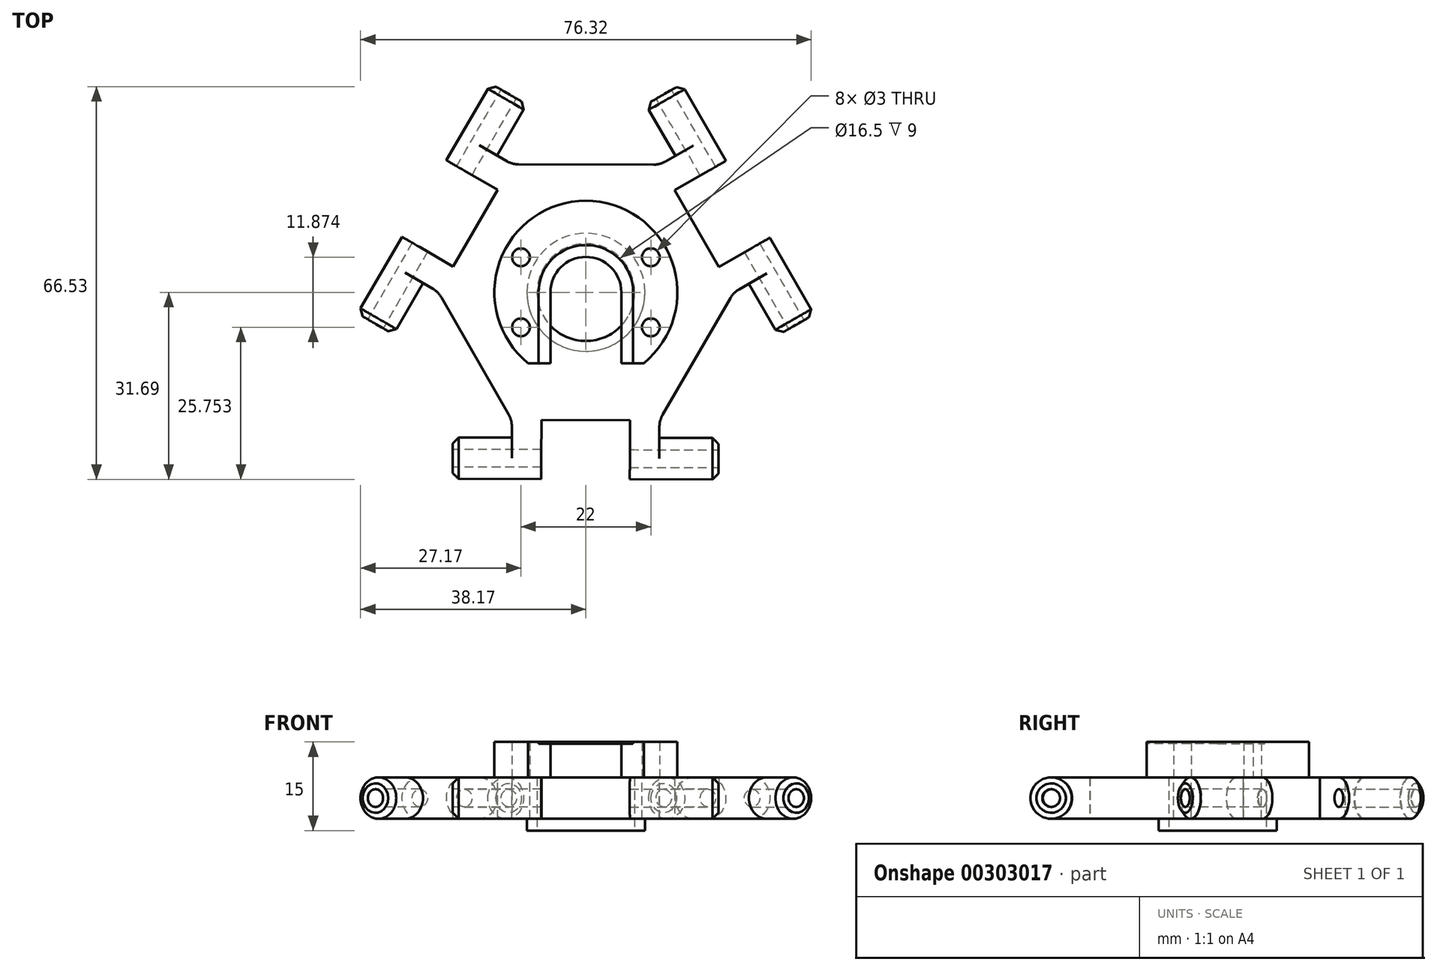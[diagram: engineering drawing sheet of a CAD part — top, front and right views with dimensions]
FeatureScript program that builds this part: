
annotation { "Feature Type Name" : "Feature", "Feature Type Description" : "" }
export const myFeature = defineFeature(function(context is Context, id is Id, definition is map)
    precondition{}
    {
        {
            var Q0;
            Q0=qCreatedBy(makeId("Top.planeOp"),FACE);
            var sketch = newSketch(context, id + "F0", { "sketchPlane" : qUnion([Q0])});
            skCircle(sketch, "E0", {"center": v(0, 0) * mm, "radius": 8.25 * mm});
            skCircle(sketch, "E1", {"center": v(0, 0) * mm, "radius": 11 * mm});
            skCircle(sketch, "E2.cCircle", {"center": v(0, 0) * mm, "radius": 11 * mm, "construction": true});
            skCircle(sketch, "E3.cCircle", {"center": v(0, 0) * mm, "radius": 21.65 * mm, "construction": true});
            skLineSegment(sketch, "E3.0", {"start": v(12.54, 21.63) * mm, "end": v(25, -0.05) * mm});
            skLineSegment(sketch, "E3.1", {"start": v(25, -0.05) * mm, "end": v(12.46, -21.67) * mm});
            skLineSegment(sketch, "E3.2", {"start": v(12.46, -21.67) * mm, "end": v(-12.54, -21.63) * mm});
            skLineSegment(sketch, "E3.3", {"start": v(-12.54, -21.63) * mm, "end": v(-25, 0.05) * mm});
            skLineSegment(sketch, "E3.4", {"start": v(-25, 0.05) * mm, "end": v(-12.46, 21.67) * mm});
            skLineSegment(sketch, "E3.5", {"start": v(-12.46, 21.67) * mm, "end": v(12.54, 21.63) * mm});
            skPoint(sketch, "E3.0.midPoint", {"position": v(18.77, 10.79) * mm});
            skSolve(sketch);
        }
        {
            var Q0;
            Q0=makeQuery(id+"F0.imprint","IMPRINT",FACE,{"disambiguationData":[TD([[makeQuery(id+"F0.imprint","IMPRINT",EDGE,{"derivedFrom":sQuery(id+"F0.wireOp",EDGE,"E1")}),-1.0]])]});
            var Q1;
            Q1=makeQuery(id+"F0.imprint","IMPRINT",FACE,{"disambiguationData":[TD([[makeQuery(id+"F0.imprint","IMPRINT",EDGE,{"derivedFrom":sQuery(id+"F0.wireOp",EDGE,"E0")}),-1.0]])]});
            extrude(context, id + "F1", {"entities" : qUnion([Q0, Q1]), "depth" : 7 * mm});
        }
        {
            var Q0;
            Q0=makeQuery(id+"F1.opExtrude","SWEPT_FACE",FACE,{"disambiguationData":[OSD([sQuery(id+"F0.wireOp",EDGE,"E3.2")])]});
            var sketch = newSketch(context, id + "F2", { "sketchPlane" : qUnion([Q0])});
            skLineSegment(sketch, "E4.bottom", {"start": v(-12.5, 7) * mm, "end": v(-7.5, 7) * mm});
            skLineSegment(sketch, "E4.top", {"start": v(-12.5, 0) * mm, "end": v(-7.5, 0) * mm});
            skLineSegment(sketch, "E4.left", {"start": v(-12.5, 7) * mm, "end": v(-12.5, 0) * mm});
            skLineSegment(sketch, "E4.right", {"start": v(-7.5, 7) * mm, "end": v(-7.5, 0) * mm});
            skLineSegment(sketch, "E5.bottom", {"start": v(12.5, 7) * mm, "end": v(7.5, 7) * mm});
            skLineSegment(sketch, "E5.top", {"start": v(12.5, 0) * mm, "end": v(7.5, 0) * mm});
            skLineSegment(sketch, "E5.left", {"start": v(12.5, 7) * mm, "end": v(12.5, 0) * mm});
            skLineSegment(sketch, "E5.right", {"start": v(7.5, 7) * mm, "end": v(7.5, 0) * mm});
            skSolve(sketch);
        }
        {
            var Q0;
            Q0=makeQuery(id+"F2.imprint","IMPRINT",FACE,{"disambiguationData":[TD([[makeQuery(id+"F2.imprint","IMPRINT",EDGE,{"derivedFrom":sQuery(id+"F2.wireOp",EDGE,"E4.bottom")}),1.0]])]});
            var Q1;
            Q1=makeQuery(id+"F2.imprint","IMPRINT",FACE,{"disambiguationData":[TD([[makeQuery(id+"F2.imprint","IMPRINT",EDGE,{"derivedFrom":sQuery(id+"F2.wireOp",EDGE,"E5.bottom")}),1.0]])]});
            extrude(context, id + "F3", {"entities" : qUnion([Q0, Q1]), "operationType" : NewBodyOperationType.ADD, "depth" : 10 * mm});
        }
        {
            var Q0;
            Q0=makeQuery(id+"F3.opExtrude","SWEPT_FACE",FACE,{"disambiguationData":[OSD([sQuery(id+"F2.wireOp",EDGE,"E4.left")])]});
            var sketch = newSketch(context, id + "F4", { "sketchPlane" : qUnion([Q0])});
            skCircle(sketch, "E6", {"center": v(28.15, 3.5) * mm, "radius": 3.5 * mm});
            skPoint(sketch, "E6.centerSnap0", {"position": v(28.15, 0) * mm});
            skPoint(sketch, "E6.centerSnap1", {"position": v(21.65, 3.5) * mm});
            skLineSegment(sketch, "E7", {"start": v(31.65, 3.5) * mm, "end": v(28.15, 3.5) * mm, "construction": true});
            skSolve(sketch);
        }
        {
            var Q0;
            {var subQ0=sQuery(id+"F4.wireOp",EDGE,"E6");var subQ1=sQuery(id+"F2.wireOp",EDGE,"E4.left");var subQ3=makeQuery(id+"F4.imprint","INTERSECT",VERTEX,{"derivedFrom":[makeQuery(id+"F3.opExtrude","CAP_EDGE",EDGE,{"disambiguationData":[OSD([subQ1])],"isStart":false}),subQ0]});Q0=makeQuery(id+"F4.imprint","IMPRINT",FACE,{"disambiguationData":[TD([[makeQuery(id+"F4.imprint","IMPRINT",EDGE,{"disambiguationData":[TD([[subQ3,-1.0]])],"derivedFrom":subQ0}),1.0]])]});}
            extrude(context, id + "F5", {"entities" : qUnion([Q0]), "operationType" : NewBodyOperationType.ADD, "depth" : 10 * mm, "offsetDistance" : 25 * mm});
        }
        {
            var Q0;
            Q0=makeQuery(id+"F5.opExtrude","CAP_FACE",FACE,{"disambiguationData":[OSD([sQuery(id+"F4.wireOp",EDGE,"E6")])],"isStart":false});
            var sketch = newSketch(context, id + "F6", { "sketchPlane" : qUnion([Q0])});
            skCircle(sketch, "E8", {"center": v(28.15, 3.5) * mm, "radius": 1.5 * mm});
            skSolve(sketch);
        }
        {
            var Q0;
            Q0=makeQuery(id+"F6.imprint","IMPRINT",FACE,{"disambiguationData":[TD([[makeQuery(id+"F6.imprint","IMPRINT",EDGE,{"derivedFrom":sQuery(id+"F6.wireOp",EDGE,"E8")}),1.0]])]});
            extrude(context, id + "F7", {"entities" : qUnion([Q0]), "operationType" : NewBodyOperationType.REMOVE, "oppositeDirection" : true, "depth" : 25 * mm});
        }
        {
            var Q0;
            Q0=makeQuery(id+"F5.opExtrude","CAP_EDGE",EDGE,{"disambiguationData":[OSD([sQuery(id+"F4.wireOp",EDGE,"E6")])],"isStart":false});
            chamfer(context, id + "F8", {"entities" : qUnion([Q0]), "width" : 1 * mm, "tangentPropagation" : true});
        }
        {
            var Q0;
            Q0=makeQuery(id+"F3.opExtrude","SWEPT_FACE",FACE,{"disambiguationData":[OSD([sQuery(id+"F2.wireOp",EDGE,"E5.left")])]});
            var sketch = newSketch(context, id + "F9", { "sketchPlane" : qUnion([Q0])});
            skCircle(sketch, "E9", {"center": v(-28.15, 3.5) * mm, "radius": 3.5 * mm});
            skPoint(sketch, "E9.centerSnap0", {"position": v(-31.65, 3.5) * mm});
            skPoint(sketch, "E9.centerSnap1", {"position": v(-28.15, 5) * mm});
            skLineSegment(sketch, "E10", {"start": v(-31.65, 3.5) * mm, "end": v(-28.15, 3.5) * mm, "construction": true});
            skSolve(sketch);
        }
        {
            var Q0;
            {var subQ0=sQuery(id+"F9.wireOp",EDGE,"E9");var subQ1=sQuery(id+"F2.wireOp",EDGE,"E5.left");var subQ4=makeQuery(id+"F9.imprint","INTERSECT",VERTEX,{"derivedFrom":[makeQuery(id+"F3.opExtrude","CAP_EDGE",EDGE,{"disambiguationData":[OSD([subQ1])],"isStart":false}),subQ0]});Q0=makeQuery(id+"F9.imprint","IMPRINT",FACE,{"disambiguationData":[TD([[makeQuery(id+"F9.imprint","IMPRINT",EDGE,{"disambiguationData":[TD([[subQ4,1.0]])],"derivedFrom":subQ0}),1.0]])]});}
            extrude(context, id + "F10", {"entities" : qUnion([Q0]), "operationType" : NewBodyOperationType.ADD, "depth" : 10 * mm, "offsetDistance" : 25 * mm});
        }
        {
            var Q0;
            Q0=makeQuery(id+"F10.opExtrude","CAP_FACE",FACE,{"disambiguationData":[OSD([sQuery(id+"F9.wireOp",EDGE,"E9")])],"isStart":false});
            var sketch = newSketch(context, id + "F11", { "sketchPlane" : qUnion([Q0])});
            skCircle(sketch, "E11", {"center": v(-28.15, 3.5) * mm, "radius": 1.5 * mm});
            skSolve(sketch);
        }
        {
            var Q0;
            Q0=makeQuery(id+"F11.imprint","IMPRINT",FACE,{"disambiguationData":[TD([[makeQuery(id+"F11.imprint","IMPRINT",EDGE,{"derivedFrom":sQuery(id+"F11.wireOp",EDGE,"E11")}),1.0]])]});
            extrude(context, id + "F12", {"entities" : qUnion([Q0]), "operationType" : NewBodyOperationType.REMOVE, "oppositeDirection" : true, "depth" : 25 * mm});
        }
        {
            var Q0;
            Q0=makeQuery(id+"F10.opExtrude","CAP_EDGE",EDGE,{"disambiguationData":[OSD([sQuery(id+"F9.wireOp",EDGE,"E9")])],"isStart":false});
            chamfer(context, id + "F13", {"entities" : qUnion([Q0]), "width" : 1 * mm, "tangentPropagation" : true});
        }
        {
            var Q0;
            Q0=makeQuery(id+"F1.opExtrude","SWEPT_FACE",FACE,{"disambiguationData":[OSD([sQuery(id+"F0.wireOp",EDGE,"E3.0")])]});
            var sketch = newSketch(context, id + "F14", { "sketchPlane" : qUnion([Q0])});
            skLineSegment(sketch, "E12.bottom", {"start": v(-12.5, 7) * mm, "end": v(-7.5, 7) * mm});
            skLineSegment(sketch, "E12.top", {"start": v(-12.5, 0) * mm, "end": v(-7.5, 0) * mm});
            skLineSegment(sketch, "E12.left", {"start": v(-12.5, 7) * mm, "end": v(-12.5, 0) * mm});
            skLineSegment(sketch, "E12.right", {"start": v(-7.5, 7) * mm, "end": v(-7.5, 0) * mm});
            skLineSegment(sketch, "E13.bottom", {"start": v(12.5, 7) * mm, "end": v(7.5, 7) * mm});
            skLineSegment(sketch, "E13.top", {"start": v(12.5, 0) * mm, "end": v(7.5, 0) * mm});
            skLineSegment(sketch, "E13.left", {"start": v(12.5, 7) * mm, "end": v(12.5, 0) * mm});
            skLineSegment(sketch, "E13.right", {"start": v(7.5, 7) * mm, "end": v(7.5, 0) * mm});
            skSolve(sketch);
        }
        {
            var Q0;
            Q0=makeQuery(id+"F14.imprint","IMPRINT",FACE,{"disambiguationData":[TD([[makeQuery(id+"F14.imprint","IMPRINT",EDGE,{"derivedFrom":sQuery(id+"F14.wireOp",EDGE,"E12.bottom")}),1.0]])]});
            var Q1;
            Q1=makeQuery(id+"F14.imprint","IMPRINT",FACE,{"disambiguationData":[TD([[makeQuery(id+"F14.imprint","IMPRINT",EDGE,{"derivedFrom":sQuery(id+"F14.wireOp",EDGE,"E13.bottom")}),1.0]])]});
            extrude(context, id + "F15", {"entities" : qUnion([Q0, Q1]), "operationType" : NewBodyOperationType.ADD, "depth" : 10 * mm});
        }
        {
            var Q0;
            Q0=makeQuery(id+"F15.opExtrude","SWEPT_FACE",FACE,{"disambiguationData":[OSD([sQuery(id+"F14.wireOp",EDGE,"E12.left")])]});
            var sketch = newSketch(context, id + "F16", { "sketchPlane" : qUnion([Q0])});
            skCircle(sketch, "E14", {"center": v(28.15, 3.5) * mm, "radius": 3.5 * mm});
            skPoint(sketch, "E14.centerSnap0", {"position": v(31.65, 3.5) * mm});
            skPoint(sketch, "E14.centerSnap1", {"position": v(28.15, 5) * mm});
            skLineSegment(sketch, "E15", {"start": v(31.65, 3.5) * mm, "end": v(28.15, 3.5) * mm, "construction": true});
            skSolve(sketch);
        }
        {
            var Q0;
            {var subQ0=sQuery(id+"F16.wireOp",EDGE,"E14");var subQ1=sQuery(id+"F14.wireOp",EDGE,"E12.left");var subQ3=makeQuery(id+"F16.imprint","INTERSECT",VERTEX,{"derivedFrom":[makeQuery(id+"F15.opExtrude","CAP_EDGE",EDGE,{"disambiguationData":[OSD([subQ1])],"isStart":false}),subQ0]});Q0=makeQuery(id+"F16.imprint","IMPRINT",FACE,{"disambiguationData":[TD([[makeQuery(id+"F16.imprint","IMPRINT",EDGE,{"disambiguationData":[TD([[subQ3,-1.0]])],"derivedFrom":subQ0}),1.0]])]});}
            extrude(context, id + "F17", {"entities" : qUnion([Q0]), "operationType" : NewBodyOperationType.ADD, "depth" : 10 * mm, "offsetDistance" : 25 * mm});
        }
        {
            var Q0;
            Q0=makeQuery(id+"F17.opExtrude","CAP_FACE",FACE,{"disambiguationData":[OSD([sQuery(id+"F16.wireOp",EDGE,"E14")])],"isStart":false});
            var sketch = newSketch(context, id + "F18", { "sketchPlane" : qUnion([Q0])});
            skCircle(sketch, "E16", {"center": v(28.15, 3.5) * mm, "radius": 1.5 * mm});
            skSolve(sketch);
        }
        {
            var Q0;
            Q0=makeQuery(id+"F18.imprint","IMPRINT",FACE,{"disambiguationData":[TD([[makeQuery(id+"F18.imprint","IMPRINT",EDGE,{"derivedFrom":sQuery(id+"F18.wireOp",EDGE,"E16")}),1.0]])]});
            extrude(context, id + "F19", {"entities" : qUnion([Q0]), "operationType" : NewBodyOperationType.REMOVE, "oppositeDirection" : true, "depth" : 25 * mm});
        }
        {
            var Q0;
            Q0=makeQuery(id+"F17.opExtrude","CAP_EDGE",EDGE,{"disambiguationData":[OSD([sQuery(id+"F16.wireOp",EDGE,"E14")])],"isStart":false});
            chamfer(context, id + "F20", {"entities" : qUnion([Q0]), "width" : 1 * mm, "tangentPropagation" : true});
        }
        {
            var Q0;
            Q0=makeQuery(id+"F15.opExtrude","SWEPT_FACE",FACE,{"disambiguationData":[OSD([sQuery(id+"F14.wireOp",EDGE,"E13.left")])]});
            var sketch = newSketch(context, id + "F21", { "sketchPlane" : qUnion([Q0])});
            skCircle(sketch, "E17", {"center": v(-28.15, 3.5) * mm, "radius": 3.5 * mm});
            skPoint(sketch, "E17.centerSnap0", {"position": v(-28.15, 5) * mm});
            skPoint(sketch, "E17.centerSnap1", {"position": v(-21.65, 3.5) * mm});
            skLineSegment(sketch, "E18", {"start": v(-31.65, 3.5) * mm, "end": v(-28.15, 3.5) * mm, "construction": true});
            skPoint(sketch, "E18.endSnap0", {"position": v(-31.65, 3.5) * mm});
            skSolve(sketch);
        }
        {
            var Q0;
            {var subQ0=sQuery(id+"F21.wireOp",EDGE,"E17");var subQ1=sQuery(id+"F14.wireOp",EDGE,"E13.left");var subQ4=makeQuery(id+"F21.imprint","INTERSECT",VERTEX,{"derivedFrom":[makeQuery(id+"F15.opExtrude","CAP_EDGE",EDGE,{"disambiguationData":[OSD([subQ1])],"isStart":false}),subQ0]});Q0=makeQuery(id+"F21.imprint","IMPRINT",FACE,{"disambiguationData":[TD([[makeQuery(id+"F21.imprint","IMPRINT",EDGE,{"disambiguationData":[TD([[subQ4,1.0]])],"derivedFrom":subQ0}),1.0]])]});}
            extrude(context, id + "F22", {"entities" : qUnion([Q0]), "operationType" : NewBodyOperationType.ADD, "depth" : 10 * mm, "offsetDistance" : 25 * mm});
        }
        {
            var Q0;
            Q0=makeQuery(id+"F22.opExtrude","CAP_FACE",FACE,{"disambiguationData":[OSD([sQuery(id+"F21.wireOp",EDGE,"E17")])],"isStart":false});
            var sketch = newSketch(context, id + "F23", { "sketchPlane" : qUnion([Q0])});
            skCircle(sketch, "E19", {"center": v(-28.15, 3.5) * mm, "radius": 1.5 * mm});
            skSolve(sketch);
        }
        {
            var Q0;
            Q0=makeQuery(id+"F23.imprint","IMPRINT",FACE,{"disambiguationData":[TD([[makeQuery(id+"F23.imprint","IMPRINT",EDGE,{"derivedFrom":sQuery(id+"F23.wireOp",EDGE,"E19")}),1.0]])]});
            extrude(context, id + "F24", {"entities" : qUnion([Q0]), "operationType" : NewBodyOperationType.REMOVE, "oppositeDirection" : true, "depth" : 25 * mm});
        }
        {
            var Q0;
            Q0=makeQuery(id+"F22.opExtrude","CAP_EDGE",EDGE,{"disambiguationData":[OSD([sQuery(id+"F21.wireOp",EDGE,"E17")])],"isStart":false});
            chamfer(context, id + "F25", {"entities" : qUnion([Q0]), "width" : 1 * mm, "tangentPropagation" : true});
        }
        {
            var Q0;
            Q0=makeQuery(id+"F1.opExtrude","SWEPT_FACE",FACE,{"disambiguationData":[OSD([sQuery(id+"F0.wireOp",EDGE,"E3.4")])]});
            var sketch = newSketch(context, id + "F26", { "sketchPlane" : qUnion([Q0])});
            skLineSegment(sketch, "E20.bottom", {"start": v(12.5, 0) * mm, "end": v(7.5, 0) * mm});
            skLineSegment(sketch, "E20.top", {"start": v(12.5, 7) * mm, "end": v(7.5, 7) * mm});
            skLineSegment(sketch, "E20.left", {"start": v(12.5, 0) * mm, "end": v(12.5, 7) * mm});
            skLineSegment(sketch, "E20.right", {"start": v(7.5, 0) * mm, "end": v(7.5, 7) * mm});
            skLineSegment(sketch, "E21.bottom", {"start": v(-12.5, 0) * mm, "end": v(-7.5, 0) * mm});
            skLineSegment(sketch, "E21.top", {"start": v(-12.5, 7) * mm, "end": v(-7.5, 7) * mm});
            skLineSegment(sketch, "E21.left", {"start": v(-12.5, 0) * mm, "end": v(-12.5, 7) * mm});
            skLineSegment(sketch, "E21.right", {"start": v(-7.5, 0) * mm, "end": v(-7.5, 7) * mm});
            skSolve(sketch);
        }
        {
            var Q0;
            Q0=makeQuery(id+"F26.imprint","IMPRINT",FACE,{"disambiguationData":[TD([[makeQuery(id+"F26.imprint","IMPRINT",EDGE,{"derivedFrom":sQuery(id+"F26.wireOp",EDGE,"E20.bottom")}),-1.0]])]});
            var Q1;
            Q1=makeQuery(id+"F26.imprint","IMPRINT",FACE,{"disambiguationData":[TD([[makeQuery(id+"F26.imprint","IMPRINT",EDGE,{"derivedFrom":sQuery(id+"F26.wireOp",EDGE,"E21.bottom")}),-1.0]])]});
            extrude(context, id + "F27", {"entities" : qUnion([Q0, Q1]), "operationType" : NewBodyOperationType.ADD, "depth" : 10 * mm});
        }
        {
            var Q0;
            Q0=makeQuery(id+"F27.opExtrude","SWEPT_FACE",FACE,{"disambiguationData":[OSD([sQuery(id+"F26.wireOp",EDGE,"E21.left")])]});
            var sketch = newSketch(context, id + "F28", { "sketchPlane" : qUnion([Q0])});
            skCircle(sketch, "E22", {"center": v(28.15, 3.5) * mm, "radius": 3.5 * mm});
            skPoint(sketch, "E22.centerSnap0", {"position": v(31.65, 3.5) * mm});
            skPoint(sketch, "E22.centerSnap1", {"position": v(28.15, 0) * mm});
            skLineSegment(sketch, "E23", {"start": v(31.65, 3.5) * mm, "end": v(28.15, 3.5) * mm, "construction": true});
            skSolve(sketch);
        }
        {
            var Q0;
            {var subQ0=sQuery(id+"F28.wireOp",EDGE,"E22");var subQ1=sQuery(id+"F26.wireOp",EDGE,"E21.left");var subQ3=makeQuery(id+"F28.imprint","INTERSECT",VERTEX,{"derivedFrom":[makeQuery(id+"F27.opExtrude","CAP_EDGE",EDGE,{"disambiguationData":[OSD([subQ1])],"isStart":false}),subQ0]});Q0=makeQuery(id+"F28.imprint","IMPRINT",FACE,{"disambiguationData":[TD([[makeQuery(id+"F28.imprint","IMPRINT",EDGE,{"disambiguationData":[TD([[subQ3,-1.0]])],"derivedFrom":subQ0}),1.0]])]});}
            extrude(context, id + "F29", {"entities" : qUnion([Q0]), "operationType" : NewBodyOperationType.ADD, "depth" : 10 * mm, "offsetDistance" : 25 * mm});
        }
        {
            var Q0;
            Q0=makeQuery(id+"F29.opExtrude","CAP_FACE",FACE,{"disambiguationData":[OSD([sQuery(id+"F28.wireOp",EDGE,"E22")])],"isStart":false});
            var sketch = newSketch(context, id + "F30", { "sketchPlane" : qUnion([Q0])});
            skCircle(sketch, "E24", {"center": v(28.15, 3.5) * mm, "radius": 1.5 * mm});
            skSolve(sketch);
        }
        {
            var Q0;
            Q0=makeQuery(id+"F30.imprint","IMPRINT",FACE,{"disambiguationData":[TD([[makeQuery(id+"F30.imprint","IMPRINT",EDGE,{"derivedFrom":sQuery(id+"F30.wireOp",EDGE,"E24")}),1.0]])]});
            extrude(context, id + "F31", {"entities" : qUnion([Q0]), "operationType" : NewBodyOperationType.REMOVE, "oppositeDirection" : true, "depth" : 25 * mm});
        }
        {
            var Q0;
            Q0=makeQuery(id+"F29.opExtrude","CAP_EDGE",EDGE,{"disambiguationData":[OSD([sQuery(id+"F28.wireOp",EDGE,"E22")])],"isStart":false});
            chamfer(context, id + "F32", {"entities" : qUnion([Q0]), "width" : 1 * mm, "tangentPropagation" : true});
        }
        {
            var Q0;
            Q0=makeQuery(id+"F27.opExtrude","SWEPT_FACE",FACE,{"disambiguationData":[OSD([sQuery(id+"F26.wireOp",EDGE,"E20.left")])]});
            var sketch = newSketch(context, id + "F33", { "sketchPlane" : qUnion([Q0])});
            skCircle(sketch, "E25", {"center": v(-28.15, 3.5) * mm, "radius": 3.5 * mm});
            skPoint(sketch, "E25.centerSnap0", {"position": v(-28.15, 5) * mm});
            skPoint(sketch, "E25.centerSnap1", {"position": v(-21.65, 3.5) * mm});
            skLineSegment(sketch, "E26", {"start": v(-31.65, 3.5) * mm, "end": v(-28.15, 3.5) * mm, "construction": true});
            skSolve(sketch);
        }
        {
            var Q0;
            {var subQ0=sQuery(id+"F33.wireOp",EDGE,"E25");var subQ1=sQuery(id+"F26.wireOp",EDGE,"E20.left");var subQ4=makeQuery(id+"F33.imprint","INTERSECT",VERTEX,{"derivedFrom":[makeQuery(id+"F27.opExtrude","CAP_EDGE",EDGE,{"disambiguationData":[OSD([subQ1])],"isStart":false}),subQ0]});Q0=makeQuery(id+"F33.imprint","IMPRINT",FACE,{"disambiguationData":[TD([[makeQuery(id+"F33.imprint","IMPRINT",EDGE,{"disambiguationData":[TD([[subQ4,1.0]])],"derivedFrom":subQ0}),1.0]])]});}
            extrude(context, id + "F34", {"entities" : qUnion([Q0]), "operationType" : NewBodyOperationType.ADD, "depth" : 10 * mm, "offsetDistance" : 25 * mm});
        }
        {
            var Q0;
            Q0=makeQuery(id+"F34.opExtrude","CAP_FACE",FACE,{"disambiguationData":[OSD([sQuery(id+"F33.wireOp",EDGE,"E25")])],"isStart":false});
            var sketch = newSketch(context, id + "F35", { "sketchPlane" : qUnion([Q0])});
            skCircle(sketch, "E27", {"center": v(-28.15, 3.5) * mm, "radius": 1.5 * mm});
            skSolve(sketch);
        }
        {
            var Q0;
            Q0=makeQuery(id+"F35.imprint","IMPRINT",FACE,{"disambiguationData":[TD([[makeQuery(id+"F35.imprint","IMPRINT",EDGE,{"derivedFrom":sQuery(id+"F35.wireOp",EDGE,"E27")}),1.0]])]});
            extrude(context, id + "F36", {"entities" : qUnion([Q0]), "operationType" : NewBodyOperationType.REMOVE, "oppositeDirection" : true, "depth" : 25 * mm});
        }
        {
            var Q0;
            Q0=makeQuery(id+"F34.opExtrude","CAP_EDGE",EDGE,{"disambiguationData":[OSD([sQuery(id+"F33.wireOp",EDGE,"E25")])],"isStart":false});
            chamfer(context, id + "F37", {"entities" : qUnion([Q0]), "width" : 1 * mm, "tangentPropagation" : true});
        }
        {
            var Q0;
            Q0=makeQuery(id+"F27.boolean.opBoolean","MERGE",FACE,{"derivedFrom":[makeQuery(id+"F15.boolean.opBoolean","MERGE",FACE,{"derivedFrom":[makeQuery(id+"F3.boolean.opBoolean","MERGE",FACE,{"derivedFrom":[makeQuery(id+"F1.opExtrude","CAP_FACE",FACE,{"disambiguationData":[OSD([sQuery(id+"F0.wireOp",EDGE,"E0"),sQuery(id+"F0.wireOp",EDGE,"E3.0"),sQuery(id+"F0.wireOp",EDGE,"E3.1"),sQuery(id+"F0.wireOp",EDGE,"E3.2"),sQuery(id+"F0.wireOp",EDGE,"E3.3"),sQuery(id+"F0.wireOp",EDGE,"E3.4"),sQuery(id+"F0.wireOp",EDGE,"E3.5")])],"isStart":false}),makeQuery(id+"F3.opExtrude","SWEPT_FACE",FACE,{"disambiguationData":[OSD([sQuery(id+"F2.wireOp",EDGE,"E4.bottom")])]}),makeQuery(id+"F3.opExtrude","SWEPT_FACE",FACE,{"disambiguationData":[OSD([sQuery(id+"F2.wireOp",EDGE,"E5.bottom")])]})]}),makeQuery(id+"F15.opExtrude","SWEPT_FACE",FACE,{"disambiguationData":[OSD([sQuery(id+"F14.wireOp",EDGE,"E12.bottom")])]}),makeQuery(id+"F15.opExtrude","SWEPT_FACE",FACE,{"disambiguationData":[OSD([sQuery(id+"F14.wireOp",EDGE,"E13.bottom")])]})]}),makeQuery(id+"F27.opExtrude","SWEPT_FACE",FACE,{"disambiguationData":[OSD([sQuery(id+"F26.wireOp",EDGE,"E20.top")])]}),makeQuery(id+"F27.opExtrude","SWEPT_FACE",FACE,{"disambiguationData":[OSD([sQuery(id+"F26.wireOp",EDGE,"E21.top")])]})]});
            var sketch = newSketch(context, id + "F38", { "sketchPlane" : qUnion([Q0])});
            skLineSegment(sketch, "E28.bottom", {"start": v(11, 5.94) * mm, "end": v(-11, 5.94) * mm, "construction": true});
            skLineSegment(sketch, "E28.top", {"start": v(11, -5.94) * mm, "end": v(-11, -5.94) * mm, "construction": true});
            skLineSegment(sketch, "E28.left", {"start": v(11, 5.94) * mm, "end": v(11, -5.94) * mm, "construction": true});
            skLineSegment(sketch, "E28.right", {"start": v(-11, 5.94) * mm, "end": v(-11, -5.94) * mm, "construction": true});
            skPoint(sketch, "E28.middle", {"position": v(0, 0) * mm});
            skCircle(sketch, "E29", {"center": v(-11, 5.94) * mm, "radius": 1.5 * mm});
            skCircle(sketch, "E30", {"center": v(11, 5.94) * mm, "radius": 1.5 * mm});
            skCircle(sketch, "E31", {"center": v(11, -5.94) * mm, "radius": 1.5 * mm});
            skCircle(sketch, "E32", {"center": v(-11, -5.94) * mm, "radius": 1.5 * mm});
            skSolve(sketch);
        }
        {
            var Q0;
            Q0=makeQuery(id+"F38.imprint","IMPRINT",FACE,{"disambiguationData":[TD([[makeQuery(id+"F38.imprint","IMPRINT",EDGE,{"derivedFrom":sQuery(id+"F38.wireOp",EDGE,"E29")}),1.0]])]});
            var Q1;
            Q1=makeQuery(id+"F38.imprint","IMPRINT",FACE,{"disambiguationData":[TD([[makeQuery(id+"F38.imprint","IMPRINT",EDGE,{"derivedFrom":sQuery(id+"F38.wireOp",EDGE,"E30")}),1.0]])]});
            var Q2;
            Q2=makeQuery(id+"F38.imprint","IMPRINT",FACE,{"disambiguationData":[TD([[makeQuery(id+"F38.imprint","IMPRINT",EDGE,{"derivedFrom":sQuery(id+"F38.wireOp",EDGE,"E31")}),1.0]])]});
            var Q3;
            Q3=makeQuery(id+"F38.imprint","IMPRINT",FACE,{"disambiguationData":[TD([[makeQuery(id+"F38.imprint","IMPRINT",EDGE,{"derivedFrom":sQuery(id+"F38.wireOp",EDGE,"E32")}),1.0]])]});
            extrude(context, id + "F39", {"entities" : qUnion([Q0, Q1, Q2, Q3]), "operationType" : NewBodyOperationType.REMOVE, "oppositeDirection" : true, "depth" : 25 * mm});
        }
        {
            var Q0;
            Q0=makeQuery(id+"F3.opExtrude","CAP_EDGE",EDGE,{"disambiguationData":[OSD([sQuery(id+"F2.wireOp",EDGE,"E4.bottom")])],"isStart":false});
            var Q1;
            Q1=makeQuery(id+"F3.opExtrude","CAP_EDGE",EDGE,{"disambiguationData":[OSD([sQuery(id+"F2.wireOp",EDGE,"E4.top")])],"isStart":false});
            var Q2;
            Q2=makeQuery(id+"F3.opExtrude","CAP_EDGE",EDGE,{"disambiguationData":[OSD([sQuery(id+"F2.wireOp",EDGE,"E5.top")])],"isStart":false});
            var Q3;
            Q3=makeQuery(id+"F3.opExtrude","CAP_EDGE",EDGE,{"disambiguationData":[OSD([sQuery(id+"F2.wireOp",EDGE,"E5.bottom")])],"isStart":false});
            var Q4;
            Q4=makeQuery(id+"F15.opExtrude","CAP_EDGE",EDGE,{"disambiguationData":[OSD([sQuery(id+"F14.wireOp",EDGE,"E12.top")])],"isStart":false});
            var Q5;
            Q5=makeQuery(id+"F15.opExtrude","CAP_EDGE",EDGE,{"disambiguationData":[OSD([sQuery(id+"F14.wireOp",EDGE,"E12.bottom")])],"isStart":false});
            var Q6;
            Q6=makeQuery(id+"F15.opExtrude","CAP_EDGE",EDGE,{"disambiguationData":[OSD([sQuery(id+"F14.wireOp",EDGE,"E13.top")])],"isStart":false});
            var Q7;
            Q7=makeQuery(id+"F15.opExtrude","CAP_EDGE",EDGE,{"disambiguationData":[OSD([sQuery(id+"F14.wireOp",EDGE,"E13.bottom")])],"isStart":false});
            var Q8;
            Q8=makeQuery(id+"F27.opExtrude","CAP_EDGE",EDGE,{"disambiguationData":[OSD([sQuery(id+"F26.wireOp",EDGE,"E21.bottom")])],"isStart":false});
            var Q9;
            Q9=makeQuery(id+"F27.opExtrude","CAP_EDGE",EDGE,{"disambiguationData":[OSD([sQuery(id+"F26.wireOp",EDGE,"E21.top")])],"isStart":false});
            var Q10;
            Q10=makeQuery(id+"F27.opExtrude","CAP_EDGE",EDGE,{"disambiguationData":[OSD([sQuery(id+"F26.wireOp",EDGE,"E20.bottom")])],"isStart":false});
            var Q11;
            Q11=makeQuery(id+"F27.opExtrude","CAP_EDGE",EDGE,{"disambiguationData":[OSD([sQuery(id+"F26.wireOp",EDGE,"E20.top")])],"isStart":false});
            fillet(context, id + "F40", {"entities" : qUnion([Q0, Q1, Q2, Q3, Q4, Q5, Q6, Q7, Q8, Q9, Q10, Q11]), "radius" : 3.5 * mm, "tangentPropagation" : true, "allowEdgeOverflow" : false});
        }
        {
            var Q0;
            Q0=makeQuery(id+"F27.boolean.opBoolean","MERGE",EDGE,{"derivedFrom":[makeQuery(id+"F1.opExtrude","SWEPT_EDGE",EDGE,{"disambiguationData":[OSD([sQuery(id+"F0.wireOp",EDGE,"E3.3"),sQuery(id+"F0.wireOp",EDGE,"E3.4")])]}),makeQuery(id+"F27.opExtrude","CAP_EDGE",EDGE,{"disambiguationData":[OSD([sQuery(id+"F26.wireOp",EDGE,"E20.left")])],"isStart":true})]});
            var Q1;
            Q1=makeQuery(id+"F3.boolean.opBoolean","MERGE",EDGE,{"derivedFrom":[makeQuery(id+"F1.opExtrude","SWEPT_EDGE",EDGE,{"disambiguationData":[OSD([sQuery(id+"F0.wireOp",EDGE,"E3.2"),sQuery(id+"F0.wireOp",EDGE,"E3.3")])]}),makeQuery(id+"F3.opExtrude","CAP_EDGE",EDGE,{"disambiguationData":[OSD([sQuery(id+"F2.wireOp",EDGE,"E4.left")])],"isStart":true})]});
            var Q2;
            Q2=makeQuery(id+"F3.opExtrude","CAP_EDGE",EDGE,{"disambiguationData":[OSD([sQuery(id+"F2.wireOp",EDGE,"E5.right")])],"isStart":true});
            var Q3;
            Q3=makeQuery(id+"F3.opExtrude","CAP_EDGE",EDGE,{"disambiguationData":[OSD([sQuery(id+"F2.wireOp",EDGE,"E4.right")])],"isStart":true});
            var Q4;
            Q4=makeQuery(id+"F3.boolean.opBoolean","MERGE",EDGE,{"derivedFrom":[makeQuery(id+"F1.opExtrude","SWEPT_EDGE",EDGE,{"disambiguationData":[OSD([sQuery(id+"F0.wireOp",EDGE,"E3.1"),sQuery(id+"F0.wireOp",EDGE,"E3.2")])]}),makeQuery(id+"F3.opExtrude","CAP_EDGE",EDGE,{"disambiguationData":[OSD([sQuery(id+"F2.wireOp",EDGE,"E5.left")])],"isStart":true})]});
            var Q5;
            Q5=makeQuery(id+"F15.boolean.opBoolean","MERGE",EDGE,{"derivedFrom":[makeQuery(id+"F1.opExtrude","SWEPT_EDGE",EDGE,{"disambiguationData":[OSD([sQuery(id+"F0.wireOp",EDGE,"E3.0"),sQuery(id+"F0.wireOp",EDGE,"E3.1")])]}),makeQuery(id+"F15.opExtrude","CAP_EDGE",EDGE,{"disambiguationData":[OSD([sQuery(id+"F14.wireOp",EDGE,"E12.left")])],"isStart":true})]});
            var Q6;
            Q6=makeQuery(id+"F15.opExtrude","CAP_EDGE",EDGE,{"disambiguationData":[OSD([sQuery(id+"F14.wireOp",EDGE,"E12.right")])],"isStart":true});
            var Q7;
            Q7=makeQuery(id+"F15.opExtrude","CAP_EDGE",EDGE,{"disambiguationData":[OSD([sQuery(id+"F14.wireOp",EDGE,"E13.right")])],"isStart":true});
            var Q8;
            Q8=makeQuery(id+"F15.boolean.opBoolean","MERGE",EDGE,{"derivedFrom":[makeQuery(id+"F1.opExtrude","SWEPT_EDGE",EDGE,{"disambiguationData":[OSD([sQuery(id+"F0.wireOp",EDGE,"E3.0"),sQuery(id+"F0.wireOp",EDGE,"E3.5")])]}),makeQuery(id+"F15.opExtrude","CAP_EDGE",EDGE,{"disambiguationData":[OSD([sQuery(id+"F14.wireOp",EDGE,"E13.left")])],"isStart":true})]});
            var Q9;
            Q9=makeQuery(id+"F27.boolean.opBoolean","MERGE",EDGE,{"derivedFrom":[makeQuery(id+"F1.opExtrude","SWEPT_EDGE",EDGE,{"disambiguationData":[OSD([sQuery(id+"F0.wireOp",EDGE,"E3.4"),sQuery(id+"F0.wireOp",EDGE,"E3.5")])]}),makeQuery(id+"F27.opExtrude","CAP_EDGE",EDGE,{"disambiguationData":[OSD([sQuery(id+"F26.wireOp",EDGE,"E21.left")])],"isStart":true})]});
            var Q10;
            Q10=makeQuery(id+"F27.opExtrude","CAP_EDGE",EDGE,{"disambiguationData":[OSD([sQuery(id+"F26.wireOp",EDGE,"E21.right")])],"isStart":true});
            var Q11;
            Q11=makeQuery(id+"F27.opExtrude","CAP_EDGE",EDGE,{"disambiguationData":[OSD([sQuery(id+"F26.wireOp",EDGE,"E20.right")])],"isStart":true});
            fillet(context, id + "F41", {"entities" : qUnion([Q0, Q1, Q2, Q3, Q4, Q5, Q6, Q7, Q8, Q9, Q10, Q11]), "radius" : 4 * mm, "tangentPropagation" : true, "allowEdgeOverflow" : false});
        }
        {
            var Q0;
            Q0=makeQuery(id+"F27.boolean.opBoolean","MERGE",FACE,{"derivedFrom":[makeQuery(id+"F15.boolean.opBoolean","MERGE",FACE,{"derivedFrom":[makeQuery(id+"F3.boolean.opBoolean","MERGE",FACE,{"derivedFrom":[makeQuery(id+"F1.opExtrude","CAP_FACE",FACE,{"disambiguationData":[OSD([sQuery(id+"F0.wireOp",EDGE,"E0"),sQuery(id+"F0.wireOp",EDGE,"E3.0"),sQuery(id+"F0.wireOp",EDGE,"E3.1"),sQuery(id+"F0.wireOp",EDGE,"E3.2"),sQuery(id+"F0.wireOp",EDGE,"E3.3"),sQuery(id+"F0.wireOp",EDGE,"E3.4"),sQuery(id+"F0.wireOp",EDGE,"E3.5")])],"isStart":false}),makeQuery(id+"F3.opExtrude","SWEPT_FACE",FACE,{"disambiguationData":[OSD([sQuery(id+"F2.wireOp",EDGE,"E4.bottom")])]}),makeQuery(id+"F3.opExtrude","SWEPT_FACE",FACE,{"disambiguationData":[OSD([sQuery(id+"F2.wireOp",EDGE,"E5.bottom")])]})]}),makeQuery(id+"F15.opExtrude","SWEPT_FACE",FACE,{"disambiguationData":[OSD([sQuery(id+"F14.wireOp",EDGE,"E12.bottom")])]}),makeQuery(id+"F15.opExtrude","SWEPT_FACE",FACE,{"disambiguationData":[OSD([sQuery(id+"F14.wireOp",EDGE,"E13.bottom")])]})]}),makeQuery(id+"F27.opExtrude","SWEPT_FACE",FACE,{"disambiguationData":[OSD([sQuery(id+"F26.wireOp",EDGE,"E20.top")])]}),makeQuery(id+"F27.opExtrude","SWEPT_FACE",FACE,{"disambiguationData":[OSD([sQuery(id+"F26.wireOp",EDGE,"E21.top")])]})]});
            var sketch = newSketch(context, id + "F42", { "sketchPlane" : qUnion([Q0])});
            skArc(sketch, "E33", {"start": v(6, 0) * mm, "mid": v(0, 6) * mm, "end": v(-6, 0) * mm});
            skArc(sketch, "E34", {"start": v(9.8, -12.01) * mm, "mid": v(0, 15.5) * mm, "end": v(-9.8, -12.01) * mm});
            skCircle(sketch, "E35", {"center": v(-11, 5.94) * mm, "radius": 1.5 * mm});
            skCircle(sketch, "E36", {"center": v(11, 5.94) * mm, "radius": 1.5 * mm});
            skCircle(sketch, "E37", {"center": v(11, -5.94) * mm, "radius": 1.5 * mm});
            skCircle(sketch, "E38", {"center": v(-11, -5.94) * mm, "radius": 1.5 * mm});
            skLineSegment(sketch, "E39", {"start": v(-6, 0) * mm, "end": v(-6, -12.01) * mm});
            skLineSegment(sketch, "E40", {"start": v(6, 0) * mm, "end": v(6, -12.01) * mm});
            skLineSegment(sketch, "E41", {"start": v(-9.8, -12.01) * mm, "end": v(-6, -12.01) * mm});
            skLineSegment(sketch, "E42.trimOffspring", {"start": v(6, -12.01) * mm, "end": v(9.8, -12.01) * mm});
            skSolve(sketch);
        }
        {
            var Q0;
            {var subQ0=sQuery(id+"F42.wireOp",EDGE,"E33");Q0=makeQuery(id+"F42.imprint","IMPRINT",FACE,{"disambiguationData":[TD([[makeQuery(id+"F42.imprint","IMPRINT",EDGE,{"derivedFrom":subQ0}),-1.0]])]});}
            var Q1;
            Q1=makeQuery(id+"F42.imprint","IMPRINT",FACE,{"disambiguationData":[TD([[makeQuery(id+"F42.imprint","IMPRINT",EDGE,{"derivedFrom":sQuery(id+"F42.wireOp",EDGE,"E34")}),1.0]])]});
            extrude(context, id + "F43", {"entities" : qUnion([Q0, Q1]), "depth" : 6 * mm});
        }
        {
            var Q0;
            Q0=makeQuery(id+"F43.opExtrude","CAP_FACE",FACE,{"disambiguationData":[OSD([sQuery(id+"F42.wireOp",EDGE,"E33"),sQuery(id+"F42.wireOp",EDGE,"E34"),sQuery(id+"F42.wireOp",EDGE,"E35"),sQuery(id+"F42.wireOp",EDGE,"E36"),sQuery(id+"F42.wireOp",EDGE,"E37"),sQuery(id+"F42.wireOp",EDGE,"E38"),sQuery(id+"F42.wireOp",EDGE,"E39"),sQuery(id+"F42.wireOp",EDGE,"E40"),sQuery(id+"F42.wireOp",EDGE,"E41"),sQuery(id+"F42.wireOp",EDGE,"E42.trimOffspring")])],"isStart":false});
            var sketch = newSketch(context, id + "F44", { "sketchPlane" : qUnion([Q0])});
            skArc(sketch, "E43", {"start": v(8, 0) * mm, "mid": v(0, 8) * mm, "end": v(-8, 0) * mm});
            skLineSegment(sketch, "E44", {"start": v(-8, 0) * mm, "end": v(-8, -12.01) * mm});
            skLineSegment(sketch, "E45", {"start": v(8, 0) * mm, "end": v(8, -12.01) * mm});
            skArc(sketch, "E46", {"start": v(6, 0) * mm, "mid": v(0, 6) * mm, "end": v(-6, 0) * mm});
            skLineSegment(sketch, "E47", {"start": v(-6, 0) * mm, "end": v(-6, -12.01) * mm});
            skLineSegment(sketch, "E48", {"start": v(-8, -12.01) * mm, "end": v(-6, -12.01) * mm});
            skLineSegment(sketch, "E49", {"start": v(6, 0) * mm, "end": v(6, -12.01) * mm});
            skLineSegment(sketch, "E50", {"start": v(6, -12.01) * mm, "end": v(8, -12.01) * mm});
            skSolve(sketch);
        }
        {
            var Q0;
            Q0=makeQuery(id+"F44.imprint","IMPRINT",FACE,{"disambiguationData":[TD([[makeQuery(id+"F44.imprint","IMPRINT",EDGE,{"derivedFrom":sQuery(id+"F44.wireOp",EDGE,"E43")}),1.0]])]});
            extrude(context, id + "F45", {"entities" : qUnion([Q0]), "operationType" : NewBodyOperationType.REMOVE, "oppositeDirection" : true, "depth" : 0.3 * mm});
        }
        {
            var Q0;
            Q0=makeQuery(id+"F27.boolean.opBoolean","MERGE",FACE,{"derivedFrom":[makeQuery(id+"F15.boolean.opBoolean","MERGE",FACE,{"derivedFrom":[makeQuery(id+"F3.boolean.opBoolean","MERGE",FACE,{"derivedFrom":[makeQuery(id+"F1.opExtrude","CAP_FACE",FACE,{"disambiguationData":[OSD([sQuery(id+"F0.wireOp",EDGE,"E0"),sQuery(id+"F0.wireOp",EDGE,"E3.0"),sQuery(id+"F0.wireOp",EDGE,"E3.1"),sQuery(id+"F0.wireOp",EDGE,"E3.2"),sQuery(id+"F0.wireOp",EDGE,"E3.3"),sQuery(id+"F0.wireOp",EDGE,"E3.4"),sQuery(id+"F0.wireOp",EDGE,"E3.5")])],"isStart":true}),makeQuery(id+"F3.opExtrude","SWEPT_FACE",FACE,{"disambiguationData":[OSD([sQuery(id+"F2.wireOp",EDGE,"E4.top")])]}),makeQuery(id+"F3.opExtrude","SWEPT_FACE",FACE,{"disambiguationData":[OSD([sQuery(id+"F2.wireOp",EDGE,"E5.top")])]})]}),makeQuery(id+"F15.opExtrude","SWEPT_FACE",FACE,{"disambiguationData":[OSD([sQuery(id+"F14.wireOp",EDGE,"E12.top")])]}),makeQuery(id+"F15.opExtrude","SWEPT_FACE",FACE,{"disambiguationData":[OSD([sQuery(id+"F14.wireOp",EDGE,"E13.top")])]})]}),makeQuery(id+"F27.opExtrude","SWEPT_FACE",FACE,{"disambiguationData":[OSD([sQuery(id+"F26.wireOp",EDGE,"E20.bottom")])]}),makeQuery(id+"F27.opExtrude","SWEPT_FACE",FACE,{"disambiguationData":[OSD([sQuery(id+"F26.wireOp",EDGE,"E21.bottom")])]})]});
            var sketch = newSketch(context, id + "F46", { "sketchPlane" : qUnion([Q0])});
            skCircle(sketch, "E51", {"center": v(0, 0) * mm, "radius": 10 * mm});
            skSolve(sketch);
        }
        {
            var Q0;
            Q0=makeQuery(id+"F46.imprint","IMPRINT",FACE,{"disambiguationData":[TD([[makeQuery(id+"F46.imprint","IMPRINT",EDGE,{"derivedFrom":sQuery(id+"F46.wireOp",EDGE,"E51")}),1.0]])]});
            extrude(context, id + "F47", {"entities" : qUnion([Q0]), "operationType" : NewBodyOperationType.ADD, "depth" : 2 * mm});
        }
    });
